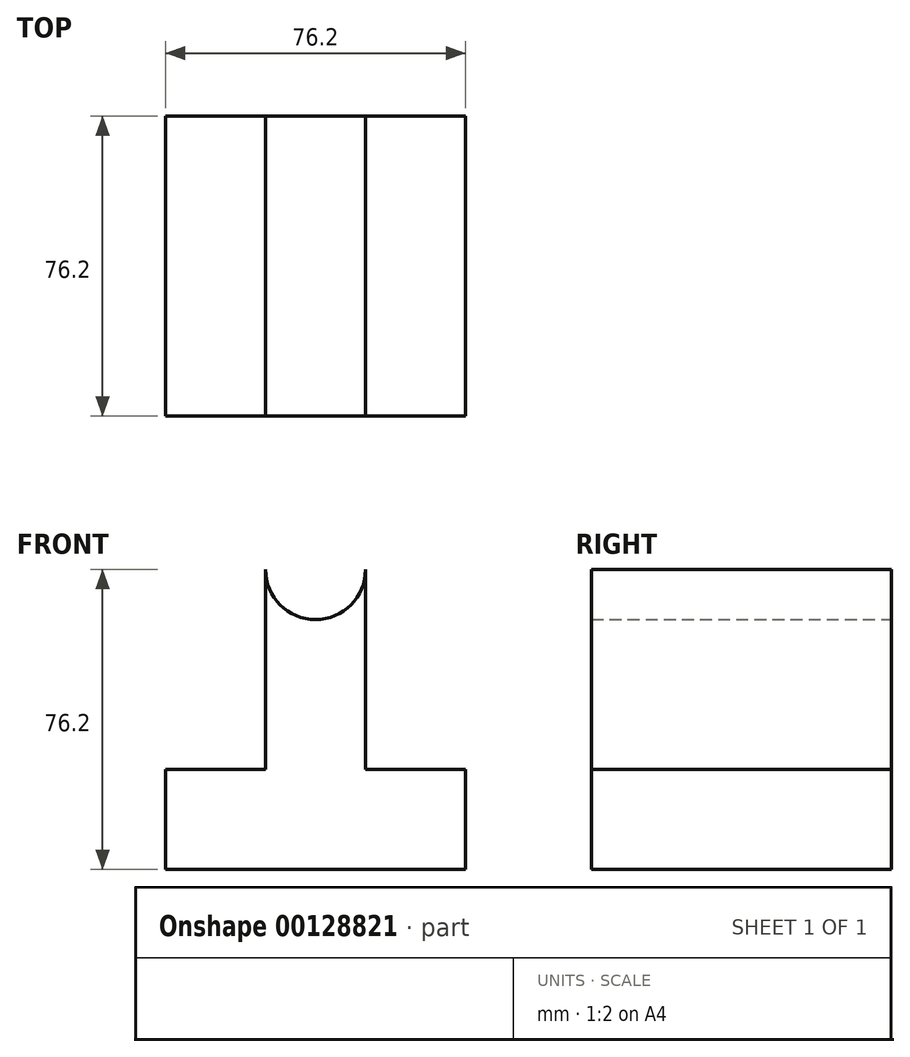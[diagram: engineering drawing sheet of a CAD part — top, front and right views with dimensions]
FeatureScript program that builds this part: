
annotation { "Feature Type Name" : "Feature", "Feature Type Description" : "" }
export const myFeature = defineFeature(function(context is Context, id is Id, definition is map)
    precondition{}
    {
        {
            var Q0;
            Q0=qCreatedBy(makeId("Front.planeOp"),FACE);
            var sketch = newSketch(context, id + "F0", { "sketchPlane" : qUnion([Q0])});
            skLineSegment(sketch, "E0", {"start": v(0, 0) * mm, "end": v(0, 25.4) * mm});
            skLineSegment(sketch, "E1", {"start": v(0, 25.4) * mm, "end": v(25.4, 25.4) * mm});
            skLineSegment(sketch, "E2", {"start": v(25.4, 25.4) * mm, "end": v(25.4, 76.2) * mm});
            skLineSegment(sketch, "E3", {"start": v(50.8, 76.2) * mm, "end": v(50.8, 25.4) * mm});
            skLineSegment(sketch, "E4", {"start": v(50.8, 25.4) * mm, "end": v(76.2, 25.4) * mm});
            skLineSegment(sketch, "E5", {"start": v(0, 0) * mm, "end": v(76.2, 0) * mm});
            skLineSegment(sketch, "E6", {"start": v(76.2, 25.4) * mm, "end": v(76.2, 0) * mm});
            skPoint(sketch, "E7.endSnap0", {"position": v(38.1, 76.2) * mm});
            skArc(sketch, "E8", {"start": v(25.4, 76.2) * mm, "mid": v(38.1, 63.5) * mm, "end": v(50.8, 76.2) * mm});
            skSolve(sketch);
        }
        {
            var Q0;
            Q0=makeQuery(id+"F0.imprint","IMPRINT",FACE,{"disambiguationData":[TD([[makeQuery(id+"F0.imprint","IMPRINT",EDGE,{"derivedFrom":sQuery(id+"F0.wireOp",EDGE,"E0")}),-1.0]])]});
            extrude(context, id + "F1", {"entities" : qUnion([Q0]), "depth" : 76.2 * mm});
        }
    });
